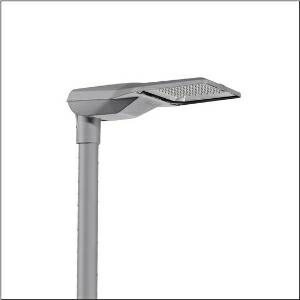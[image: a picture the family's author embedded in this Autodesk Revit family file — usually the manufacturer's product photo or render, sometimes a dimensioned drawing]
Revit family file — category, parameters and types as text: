
# Revit family: streetlight_sl_21_iq_midi___st1_0ab_5xe3m31d08nb_cbc2
name_source: partatom
category: Lighting Fixtures
units: mm (PartAtom-declared; Revit-internal decimal feet)

## family parameters
Cut with Voids When Loaded = No
Host = Face
Light Source = No
Part Type = Normal
Room Calculation Point = No
Round Connector Dimension = Use Diameter
Shared = No

## types (1)
- --- (1 x LED, 20440 lm, 155.5 W, 3000K)
    Apparent Load = 155 VA
    CIE Flux Codes = 40 74 97 100 100
    Color Rendering = 70
    Color Temperature = 3000K
    Default Elevation = 1800 mm
    Description = Streetlight SL 21 iQ midi, mast luminaire, primary light control with lens, of PMMA, primary optical cover: cover, of toughened safety glass, transparent, light distribution: ST1.0aB, light emission: direct distribution, primary light characteristic: asymmetric, installation type: post-top, side-entry, LED, High Power LED, rated luminous flux: 20.440lm, luminous efficacy: 131lm/W, light colour: 730, colour temperature: 3000K, control gear: iQ-Comfort, control: Auto-Match, Temp-Guard, Lumen-Switch, Night-Set, Smart-Wire, Light-Fading, Desk-Remote (wireless, voltage-free reading and setting of iQ features in the workshop via application-optimized NFC function/RFID function), optimised constant luminous flux control (CLO 2.0), pre-setting: linear dimming characteristic, mains connection: 230..240V, AC, 50/60Hz, start of lifetime: 156W, end of service life: 162W, reduction: 69W, luminaire housing, of diecast aluminium, powder-coated, Siteco® metallic grey (DB 702S), corrosivity category C5 mid according to DIN EN ISO 12944, please order mast flange separately, inclination adjustable: 0°, 5°, 10°, 15°, sealing non-destructively replaceable, multi-level sealing system, length: 644mm, width: 335mm, height: 110mm, mast flange for spigot size: 42mm (side-entry): 5XC10008XM4, 60/48mm (side-entry/post-top): 5XC10108XM2, 76/60mm (side-entry/post-top): 5XC10108XM1, mounting height: 4..8m, protection rating (complete): IP66, insulation class (complete): insulation class II (safety insulation), certification: CE, ENEC, ENEC+, VDE, impact resistance: IK10, permissible operating ambient temperature for outdoor applications: -40..+50°C, standard-compliant lighting for roads and squares, packaging unit: 1 piece

Light Distribution: ST1.0aB
    Height = 111 mm
    Lamp = 1 x LED
    Lamp Light Flux = 20440 lm
    Lamp Power = 155.5 W
    Lamp count = 1
    Length = 644 mm
    Luminous efficacy = 131 lm/W
    Manufacturer = Siteco
    ModVariant = No
    Model = 5XE3M31D08NB
    Number of Poles = 1
    OnlyDefault = Yes
    Power Factor = 1
    Product Name = Streetlight SL 21 iQ midi | ST1.0aB
    Product group = mast luminaire | pylon top
    ProductGroupID = 6100
    Protection Class = Protection class II
    Protection Degree = IP 66
    RLX_Detail_Level = 1
    RLX_Emergency_Light_Flux = 0 lm
    RLX_Emergency_Type = 0
    RLX_Emergency_Type_DB = No
    RlxData = <blob elided: 27193 chars, md5=1f8341d9>
    Socket = socket
    Standby Power = 0 W
    System Light Flux = 20440 lm
    System Power = 155 W
    Type Comments = factory setting: luminous flux: 100 % | dim-lin: 254 | 823 mA
    Type Image = l_1004298.jpg
    URL = http://relux.com
    VarID = @adj_168262
    Voltage = 0 V
    Weight = 0.00 kg
    Width = 336 mm

## geometry (parser evidence)
native form markers: Blend x4, Sweep x12
no freeform markers — native parametric forms only
